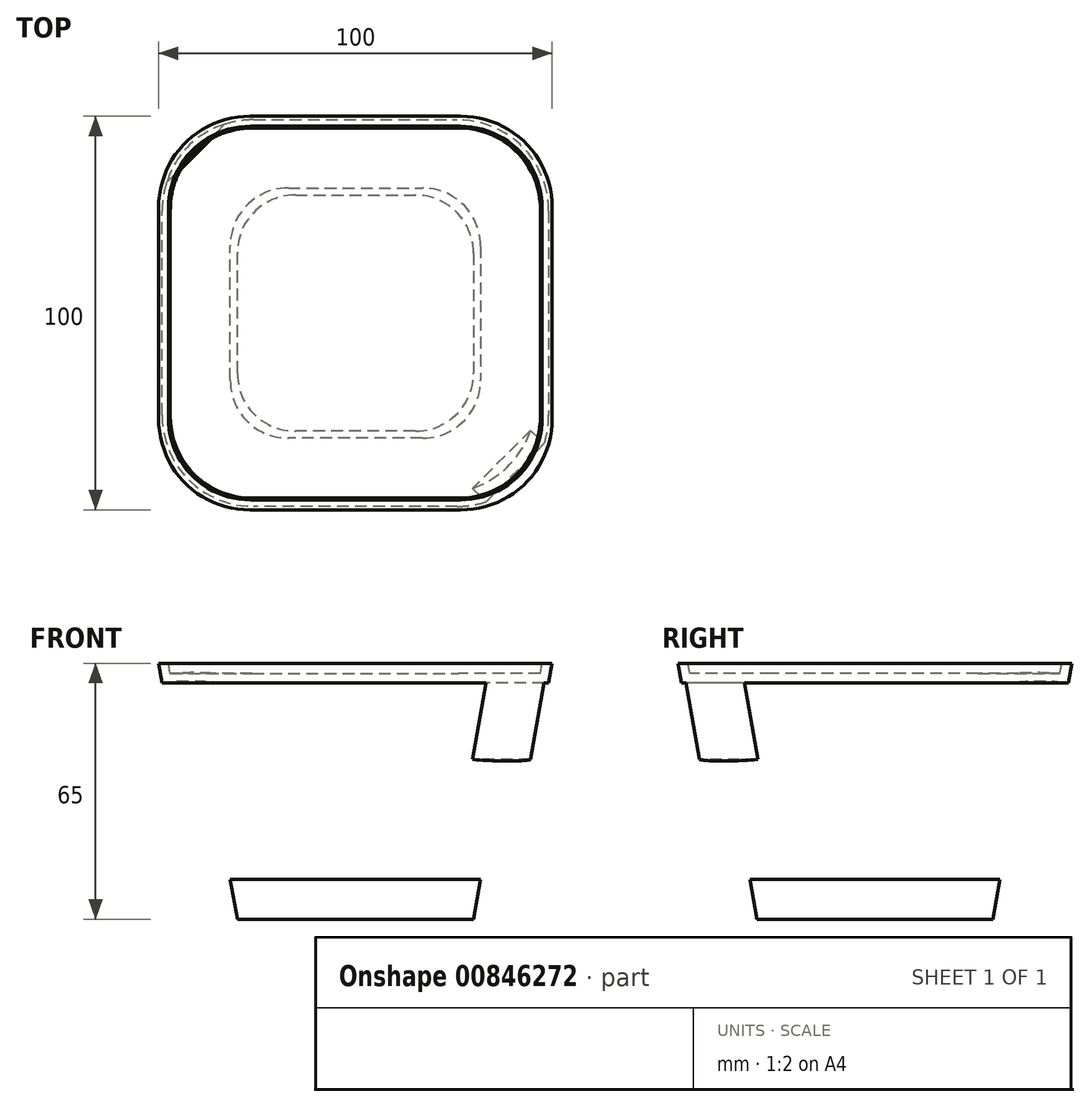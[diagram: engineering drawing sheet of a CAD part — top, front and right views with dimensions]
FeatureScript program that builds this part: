
annotation { "Feature Type Name" : "Feature", "Feature Type Description" : "" }
export const myFeature = defineFeature(function(context is Context, id is Id, definition is map)
    precondition{}
    {
        {
            var Q0;
            Q0=qCreatedBy(makeId("Top.planeOp"),FACE);
            var sketch = newSketch(context, id + "F0", { "sketchPlane" : qUnion([Q0])});
            skLineSegment(sketch, "E0.bottom", {"start": v(30, 30) * mm, "end": v(-30, 30) * mm});
            skLineSegment(sketch, "E0.top", {"start": v(30, -30) * mm, "end": v(-30, -30) * mm});
            skLineSegment(sketch, "E0.left", {"start": v(30, 30) * mm, "end": v(30, -30) * mm});
            skLineSegment(sketch, "E0.right", {"start": v(-30, 30) * mm, "end": v(-30, -30) * mm});
            skPoint(sketch, "E0.middle", {"position": v(0, 0) * mm});
            skSolve(sketch);
        }
        {
            var Q0;
            Q0 = qSketchRegion(id + "F0", true);
            extrude(context, id + "F1", {"entities" : qUnion([Q0]), "depth" : 60 * mm, "offsetDistance" : 25 * mm, "hasDraft" : true, "draftAngle" : 10 * degree});
        }
        {
            var Q0;
            Q0=qCreatedBy(makeId("Top.planeOp"),FACE);
            cPlane(context, id + "F2", {"entities" : qUnion([Q0]), "cplaneType" : CPlaneType.OFFSET, "offset" : 65 * mm, "width" : 150 * mm, "height" : 150 * mm});
        }
        {
            var Q0;
            Q0=qCreatedBy(id+"F2.planeOp",FACE);
            var sketch = newSketch(context, id + "F3", { "sketchPlane" : qUnion([Q0])});
            skLineSegment(sketch, "E1.bottom", {"start": v(50, 50) * mm, "end": v(-50, 50) * mm});
            skLineSegment(sketch, "E1.top", {"start": v(50, -50) * mm, "end": v(-50, -50) * mm});
            skLineSegment(sketch, "E1.left", {"start": v(50, 50) * mm, "end": v(50, -50) * mm});
            skLineSegment(sketch, "E1.right", {"start": v(-50, 50) * mm, "end": v(-50, -50) * mm});
            skPoint(sketch, "E1.middle", {"position": v(0, 0) * mm});
            skSolve(sketch);
        }
        {
            var Q0;
            Q0=makeQuery(id+"F3.imprint","IMPRINT",FACE,{"disambiguationData":[TD([[makeQuery(id+"F3.imprint","IMPRINT",EDGE,{"derivedFrom":sQuery(id+"F3.wireOp",EDGE,"E1.bottom")}),1.0]])]});
            extrude(context, id + "F4", {"entities" : qUnion([Q0]), "oppositeDirection" : true, "depth" : 40 * mm, "offsetDistance" : 25 * mm, "hasDraft" : true, "draftAngle" : 10 * degree, "draftPullDirection" : true});
        }
        {
            var Q0;
            Q0=makeQuery(id+"F1.opExtrude","CAP_VERTEX",VERTEX,{"disambiguationData":[OSD([sQuery(id+"F0.wireOp",EDGE,"E0.bottom"),sQuery(id+"F0.wireOp",EDGE,"E0.right")])],"isStart":false});
            var Q1;
            Q1=makeQuery(id+"F1.opExtrude","CAP_VERTEX",VERTEX,{"disambiguationData":[OSD([sQuery(id+"F0.wireOp",EDGE,"E0.top"),sQuery(id+"F0.wireOp",EDGE,"E0.left")])],"isStart":false});
            var Q2;
            Q2=makeQuery(id+"F1.opExtrude","CAP_VERTEX",VERTEX,{"disambiguationData":[OSD([sQuery(id+"F0.wireOp",EDGE,"E0.top"),sQuery(id+"F0.wireOp",EDGE,"E0.left")])],"isStart":true});
            cPlane(context, id + "F5", {"entities" : qUnion([Q0, Q1, Q2]), "cplaneType" : CPlaneType.THREE_POINT, "offset" : 25 * mm, "width" : 150 * mm, "height" : 150 * mm});
        }
        {
            var Q0;
            Q0=qCreatedBy(id+"F5.planeOp",FACE);
            var sketch = newSketch(context, id + "F6", { "sketchPlane" : qUnion([Q0])});
            skLineSegment(sketch, "E2", {"start": v(-57.39, 60) * mm, "end": v(52.55, 40.6) * mm});
            skLineSegment(sketch, "E3", {"start": v(52.55, 40.6) * mm, "end": v(57.39, 60) * mm});
            skLineSegment(sketch, "E4", {"start": v(57.39, 60) * mm, "end": v(-57.39, 60) * mm});
            skLineSegment(sketch, "E5", {"start": v(-57.39, 60) * mm, "end": v(-90.39, 65.82) * mm});
            skLineSegment(sketch, "E6", {"start": v(-90.39, 65.82) * mm, "end": v(-90.39, 10.15) * mm});
            skLineSegment(sketch, "E7", {"start": v(-90.39, 10.15) * mm, "end": v(92.88, 10.15) * mm});
            skLineSegment(sketch, "E8", {"start": v(92.88, 10.15) * mm, "end": v(92.88, 33.48) * mm});
            skLineSegment(sketch, "E9", {"start": v(92.88, 33.48) * mm, "end": v(52.55, 40.6) * mm});
            skSolve(sketch);
        }
        {
            var Q0;
            Q0=makeQuery(id+"F6.imprint","IMPRINT",FACE,{"disambiguationData":[TD([[makeQuery(id+"F6.imprint","IMPRINT",EDGE,{"derivedFrom":sQuery(id+"F6.wireOp",EDGE,"E2")}),1.0]])]});
            extrude(context, id + "F7", {"entities" : qUnion([Q0]), "operationType" : NewBodyOperationType.REMOVE, "endBound" : BoundingType.SYMMETRIC, "oppositeDirection" : true, "depth" : 120 * mm, "offsetDistance" : 25 * mm});
        }
        {
            var Q0;
            Q0=makeQuery(id+"F6.imprint","IMPRINT",FACE,{"disambiguationData":[TD([[makeQuery(id+"F6.imprint","IMPRINT",EDGE,{"derivedFrom":sQuery(id+"F6.wireOp",EDGE,"E2")}),-1.0]])]});
            extrude(context, id + "F8", {"entities" : qUnion([Q0]), "operationType" : NewBodyOperationType.REMOVE, "endBound" : BoundingType.SYMMETRIC, "depth" : 150 * mm, "offsetDistance" : 25 * mm});
        }
        {
            var Q0;
            Q0=makeQuery(id+"F1.opExtrude","SWEPT_EDGE",EDGE,{"disambiguationData":[OSD([sQuery(id+"F0.wireOp",EDGE,"E0.top"),sQuery(id+"F0.wireOp",EDGE,"E0.right")])]});
            var Q1;
            Q1=makeQuery(id+"F1.opExtrude","SWEPT_EDGE",EDGE,{"disambiguationData":[OSD([sQuery(id+"F0.wireOp",EDGE,"E0.bottom"),sQuery(id+"F0.wireOp",EDGE,"E0.right")])]});
            var Q2;
            Q2=makeQuery(id+"F1.opExtrude","SWEPT_EDGE",EDGE,{"disambiguationData":[OSD([sQuery(id+"F0.wireOp",EDGE,"E0.bottom"),sQuery(id+"F0.wireOp",EDGE,"E0.left")])]});
            var Q3;
            Q3=makeQuery(id+"F1.opExtrude","SWEPT_EDGE",EDGE,{"disambiguationData":[OSD([sQuery(id+"F0.wireOp",EDGE,"E0.top"),sQuery(id+"F0.wireOp",EDGE,"E0.left")])]});
            fillet(context, id + "F9", {"entities" : qUnion([Q0, Q1, Q2, Q3]), "radius" : 15 * mm, "tangentPropagation" : true, "allowEdgeOverflow" : false});
        }
        {
            var Q0;
            Q0=makeQuery(id+"F4.opExtrude","SWEPT_EDGE",EDGE,{"disambiguationData":[OSD([sQuery(id+"F3.wireOp",EDGE,"E1.top"),sQuery(id+"F3.wireOp",EDGE,"E1.left")])]});
            var Q1;
            Q1=makeQuery(id+"F4.opExtrude","SWEPT_EDGE",EDGE,{"disambiguationData":[OSD([sQuery(id+"F3.wireOp",EDGE,"E1.bottom"),sQuery(id+"F3.wireOp",EDGE,"E1.left")])]});
            var Q2;
            Q2=makeQuery(id+"F4.opExtrude","SWEPT_EDGE",EDGE,{"disambiguationData":[OSD([sQuery(id+"F3.wireOp",EDGE,"E1.top"),sQuery(id+"F3.wireOp",EDGE,"E1.right")])]});
            var Q3;
            Q3=makeQuery(id+"F4.opExtrude","SWEPT_EDGE",EDGE,{"disambiguationData":[OSD([sQuery(id+"F3.wireOp",EDGE,"E1.bottom"),sQuery(id+"F3.wireOp",EDGE,"E1.right")])]});
            fillet(context, id + "F10", {"entities" : qUnion([Q0, Q1, Q2, Q3]), "radius" : 23.6 * mm, "tangentPropagation" : true, "allowEdgeOverflow" : false});
        }
        {
            var Q0;
            Q0=makeQuery(id+"F4.opExtrude","CAP_FACE",FACE,{"disambiguationData":[OSD([sQuery(id+"F3.wireOp",EDGE,"E1.bottom"),sQuery(id+"F3.wireOp",EDGE,"E1.top"),sQuery(id+"F3.wireOp",EDGE,"E1.left"),sQuery(id+"F3.wireOp",EDGE,"E1.right")])],"isStart":true});
            shell(context, id + "F11", {"entities" : qUnion([Q0]), "thickness" : 2.5 * mm});
        }
    });
